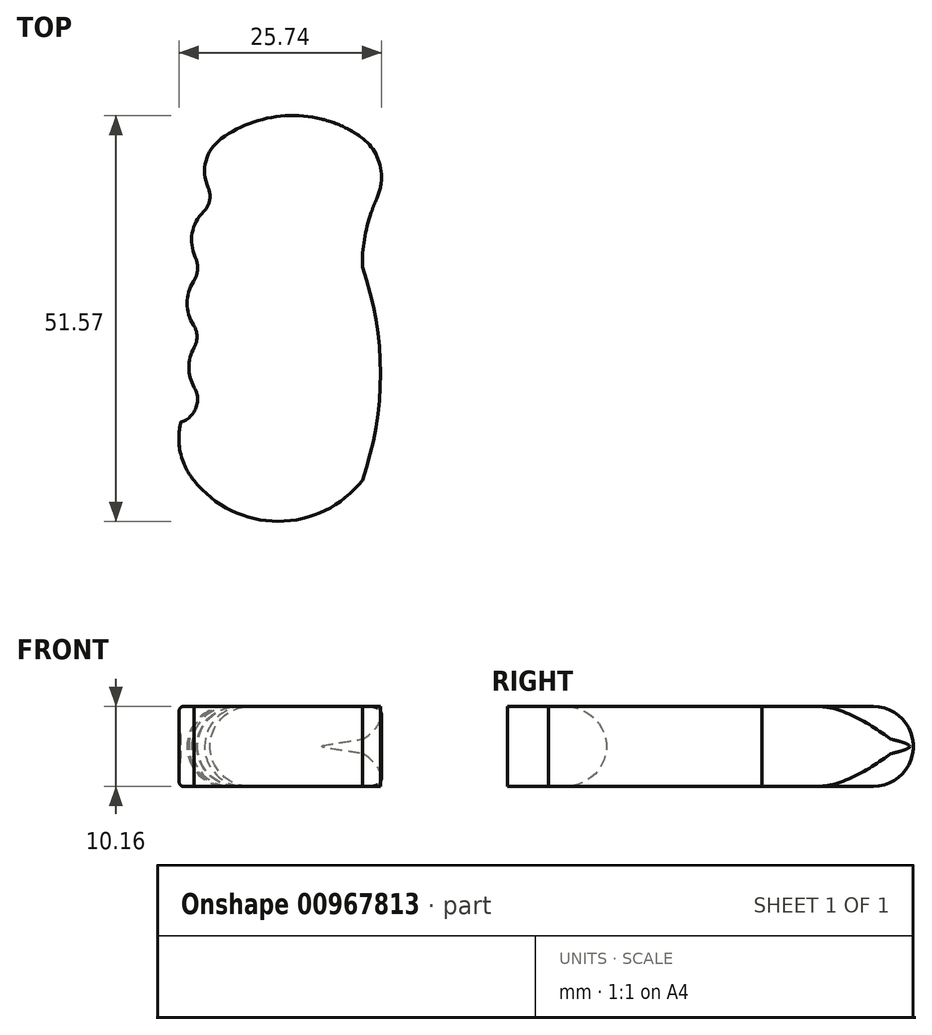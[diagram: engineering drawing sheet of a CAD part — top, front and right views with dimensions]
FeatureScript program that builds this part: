
annotation { "Feature Type Name" : "Feature", "Feature Type Description" : "" }
export const myFeature = defineFeature(function(context is Context, id is Id, definition is map)
    precondition{}
    {
        {
            var Q0;
            Q0=qCreatedBy(makeId("Top.planeOp"),FACE);
            var sketch = newSketch(context, id + "F0", { "sketchPlane" : qUnion([Q0])});
            skArc(sketch, "E0", {"start": v(-14.66, 3.04) * mm, "mid": v(-12.55, 6.22) * mm, "end": v(-15.2, 8.94) * mm});
            skArc(sketch, "E1", {"start": v(-15.58, 11.15) * mm, "mid": v(-12.66, 13.34) * mm, "end": v(-14.47, 16.5) * mm});
            skArc(sketch, "E2", {"start": v(-14.66, 19.63) * mm, "mid": v(-12.52, 22.68) * mm, "end": v(-14.66, 25.72) * mm});
            skArc(sketch, "E3", {"start": v(-14.66, 29.22) * mm, "mid": v(-11.16, 30.67) * mm, "end": v(-12.52, 34.2) * mm});
            skPoint(sketch, "E3.endSnap0", {"position": v(-12.52, 22.68) * mm});
            skArc(sketch, "E4", {"start": v(3.23, 41.57) * mm, "mid": v(-4.58, 41.44) * mm, "end": v(-11.34, 37.52) * mm});
            skArc(sketch, "E5", {"start": v(8.12, 39.35) * mm, "mid": v(5.78, 40.69) * mm, "end": v(3.23, 41.57) * mm});
            skArc(sketch, "E6", {"start": v(10.26, 31.5) * mm, "mid": v(8.84, 27.24) * mm, "end": v(8.4, 22.77) * mm});
            skPoint(sketch, "E6.endSnap0", {"position": v(8.4, 39.15) * mm});
            skArc(sketch, "E7", {"start": v(8.4, -4.33) * mm, "mid": v(10.7, 9.22) * mm, "end": v(8.4, 22.77) * mm});
            skArc(sketch, "E8", {"start": v(-13, -4.33) * mm, "mid": v(-2.3, -9.56) * mm, "end": v(8.4, -4.33) * mm});
            skPoint(sketch, "E9.visualSharp", {"position": v(12.26, 34.94) * mm});
            skArc(sketch, "E9.filletArc", {"start": v(10.26, 31.5) * mm, "mid": v(10.61, 35.8) * mm, "end": v(8.12, 39.35) * mm});
            skArc(sketch, "E10", {"start": v(-14.66, 3.04) * mm, "mid": v(-14.7, -0.84) * mm, "end": v(-13, -4.33) * mm});
            skArc(sketch, "E11", {"start": v(-15.58, 11.15) * mm, "mid": v(-15.74, 9.99) * mm, "end": v(-15.2, 8.94) * mm});
            skArc(sketch, "E12", {"start": v(-14.66, 19.63) * mm, "mid": v(-15.07, 18.04) * mm, "end": v(-14.47, 16.5) * mm});
            skArc(sketch, "E13", {"start": v(-14.66, 29.22) * mm, "mid": v(-15.02, 27.47) * mm, "end": v(-14.66, 25.72) * mm});
            skArc(sketch, "E14", {"start": v(-11.34, 37.52) * mm, "mid": v(-12.25, 35.97) * mm, "end": v(-12.52, 34.2) * mm});
            skSolve(sketch);
        }
        {
            var Q0;
            Q0 = qSketchRegion(id + "F0", true);
            extrude(context, id + "F1", {"entities" : qUnion([Q0]), "depth" : 5.08 * mm, "offsetDistance" : 25.4 * mm});
        }
        {
            var Q0;
            Q0=makeQuery(id+"F1.opExtrude","CAP_EDGE",EDGE,{"disambiguationData":[OSD([sQuery(id+"F0.wireOp",EDGE,"E2")])],"isStart":false});
            var Q1;
            Q1=makeQuery(id+"F1.opExtrude","CAP_EDGE",EDGE,{"disambiguationData":[OSD([sQuery(id+"F0.wireOp",EDGE,"E3")])],"isStart":false});
            var Q2;
            Q2=makeQuery(id+"F1.opExtrude","CAP_EDGE",EDGE,{"disambiguationData":[OSD([sQuery(id+"F0.wireOp",EDGE,"E1")])],"isStart":false});
            var Q3;
            Q3=makeQuery(id+"F1.opExtrude","CAP_EDGE",EDGE,{"disambiguationData":[OSD([sQuery(id+"F0.wireOp",EDGE,"E0")])],"isStart":false});
            fillet(context, id + "F2", {"entities" : qUnion([Q0, Q1, Q2, Q3]), "radius" : 5.08 * mm, "tangentPropagation" : true, "allowEdgeOverflow" : false});
        }
        {
            var Q0;
            Q0=makeQuery(id+"F1.opExtrude","SWEPT_BODY",BODY,{"disambiguationData":[OSD([sQuery(id+"F0.wireOp",EDGE,"E0"),sQuery(id+"F0.wireOp",EDGE,"E1"),sQuery(id+"F0.wireOp",EDGE,"E2"),sQuery(id+"F0.wireOp",EDGE,"E3"),sQuery(id+"F0.wireOp",EDGE,"E4"),sQuery(id+"F0.wireOp",EDGE,"E5"),sQuery(id+"F0.wireOp",EDGE,"E6"),sQuery(id+"F0.wireOp",EDGE,"E7"),sQuery(id+"F0.wireOp",EDGE,"E8"),sQuery(id+"F0.wireOp",EDGE,"E9.filletArc"),sQuery(id+"F0.wireOp",EDGE,"E10"),sQuery(id+"F0.wireOp",EDGE,"E11"),sQuery(id+"F0.wireOp",EDGE,"E12"),sQuery(id+"F0.wireOp",EDGE,"E13"),sQuery(id+"F0.wireOp",EDGE,"E14")])]});
            var Q1;
            Q1=qCreatedBy(makeId("Top.planeOp"),FACE);
            mirror(context, id + "F3", {"operationType" : NewBodyOperationType.ADD, "entities" : qUnion([Q0]), "mirrorPlane" : qUnion([Q1])});
        }
        {
            var Q0;
            Q0=makeQuery(id+"F1.opExtrude","CAP_EDGE",EDGE,{"disambiguationData":[OSD([sQuery(id+"F0.wireOp",EDGE,"E4")])],"isStart":false});
            fillet(context, id + "F4", {"entities" : qUnion([Q0]), "radius" : 5.08 * mm, "tangentPropagation" : true, "allowEdgeOverflow" : false});
        }
        {
            var Q0;
            Q0=makeQuery(id+"F2.opFillet","BLEND_EDGE",EDGE,{"blendedFrom":[makeQuery(id+"F1.opExtrude","CAP_EDGE",EDGE,{"disambiguationData":[OSD([sQuery(id+"F0.wireOp",EDGE,"E2")])],"isStart":false}),makeQuery(id+"F1.opExtrude","CAP_EDGE",EDGE,{"disambiguationData":[OSD([sQuery(id+"F0.wireOp",EDGE,"E3")])],"isStart":false})],"blendedInto":[]});
            var Q1;
            Q1=makeQuery(id+"F2.opFillet","BLEND_EDGE",EDGE,{"blendedFrom":[makeQuery(id+"F1.opExtrude","CAP_EDGE",EDGE,{"disambiguationData":[OSD([sQuery(id+"F0.wireOp",EDGE,"E1")])],"isStart":false}),makeQuery(id+"F1.opExtrude","CAP_EDGE",EDGE,{"disambiguationData":[OSD([sQuery(id+"F0.wireOp",EDGE,"E2")])],"isStart":false})],"blendedInto":[]});
            var Q2;
            Q2=makeQuery(id+"F2.opFillet","BLEND_EDGE",EDGE,{"blendedFrom":[makeQuery(id+"F1.opExtrude","CAP_EDGE",EDGE,{"disambiguationData":[OSD([sQuery(id+"F0.wireOp",EDGE,"E0")])],"isStart":false}),makeQuery(id+"F1.opExtrude","CAP_EDGE",EDGE,{"disambiguationData":[OSD([sQuery(id+"F0.wireOp",EDGE,"E1")])],"isStart":false})],"blendedInto":[]});
            fillet(context, id + "F5", {"entities" : qUnion([Q0, Q1, Q2]), "radius" : 5.08 * mm, "tangentPropagation" : true, "allowEdgeOverflow" : false});
        }
    });
